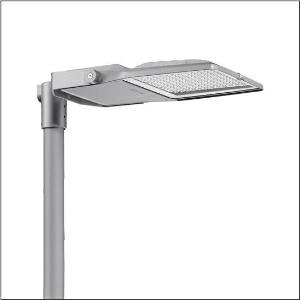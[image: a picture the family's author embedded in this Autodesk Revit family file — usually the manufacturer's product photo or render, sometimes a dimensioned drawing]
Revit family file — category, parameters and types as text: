
# Revit family: floodlight_fl_21_iq_midi___pl43_5xa7781f4a3a_cde7
name_source: partatom
category: Lighting Fixtures
units: mm (PartAtom-declared; Revit-internal decimal feet)

## family parameters
Cut with Voids When Loaded = No
Host = Face
Light Source = No
Part Type = Normal
Room Calculation Point = No
Round Connector Dimension = Use Diameter
Shared = No

## types (1)
- --- (1 x LED, 38290 lm, 270.2 W, 4000K)
    Apparent Load = 270 VA
    CIE Flux Codes = 27 78 99 100 100
    Color Rendering = 70
    Color Temperature = 4000K
    Default Elevation = 1800 mm
    Description = Floodlight FL 21 iQ midi, floodlight, primary light control with lens, of PMMA, primary optical cover: protective disc, of toughened safety glass, transparent, light distribution: PL43, light emission: direct distribution, installation type: surface-mounted, LED, High Power LED, rated luminous flux: 38.290lm, luminous efficacy: 142lm/W, light colour: 740, colour temperature: 4000K, control gear: ECG iQ, control: optimised constant luminous flux control (CLO 2.0), Desk-Remote (wireless, voltage-free reading and setting of iQ features in the workshop via application-optimized NFC function/RFID function), Light-Fading, Smart-Wire, Night-Set, Lumen-Switch, Temp-Guard, Auto-Match, with terminal, 6-pole, mains connection: 220..240V, AC, 50/60Hz, start of lifetime: 270W, end of service life: 287W, reduction: 118W, luminaire housing, of diecast aluminium, powder-coated, Siteco® metallic grey (DB 702S), corrosivity category C5 mid according to DIN EN ISO 12944, sealing non-destructively replaceable, please order mast flange separately, mast bracket, of steel, galvanised, powder-coated, Siteco® metallic grey (DB 702S), protection rating (complete): IP66, insulation class (complete): insulation class II (safety insulation), certification: CE, protection symbol: D, impact resistance: IK08, permissible operating ambient temperature: -40..+40°C, permissible operating ambient temperature for outdoor applications: -40..+50°C, standard: DIN EN 12944, LABS conformity tested according to VDMA 24364:2018-05, packaging unit: 1 piece

Light Distribution: PL43
    Height = 76 mm
    Lamp = 1 x LED
    Lamp Light Flux = 38290 lm
    Lamp Power = 270.2 W
    Lamp count = 1
    Length = 657 mm
    Luminous efficacy = 142 lm/W
    Manufacturer = Siteco
    ModVariant = No
    Model = 5XA7781F4A3A
    Number of Poles = 1
    OnlyDefault = Yes
    Power Factor = 1
    Product Name = Floodlight FL 21 iQ midi | PL43
    Product group = floodlight | pylon annexe
    ProductGroupID = 6200
    Protection Class = Protection class II
    Protection Degree = IP 66
    RLX_Detail_Level = 1
    RLX_Emergency_Light_Flux = 0 lm
    RLX_Emergency_Type = 0
    RLX_Emergency_Type_DB = No
    RlxData = <blob elided: 153577 chars, md5=b9ad9a07>
    Socket = socket
    Standby Power = 0 W
    System Light Flux = 38290 lm
    System Power = 270 W
    Type Comments = factory setting: luminous flux: 100 % | dim-lin: 254 | 620 mA
    Type Image = l_1007123.jpg
    URL = http://relux.com
    VarID = @adj_034939
    Voltage = 0 V
    Weight = 0.00 kg
    Width = 442 mm

## geometry (parser evidence)
native form markers: Blend x4, Sweep x12
no freeform markers — native parametric forms only
